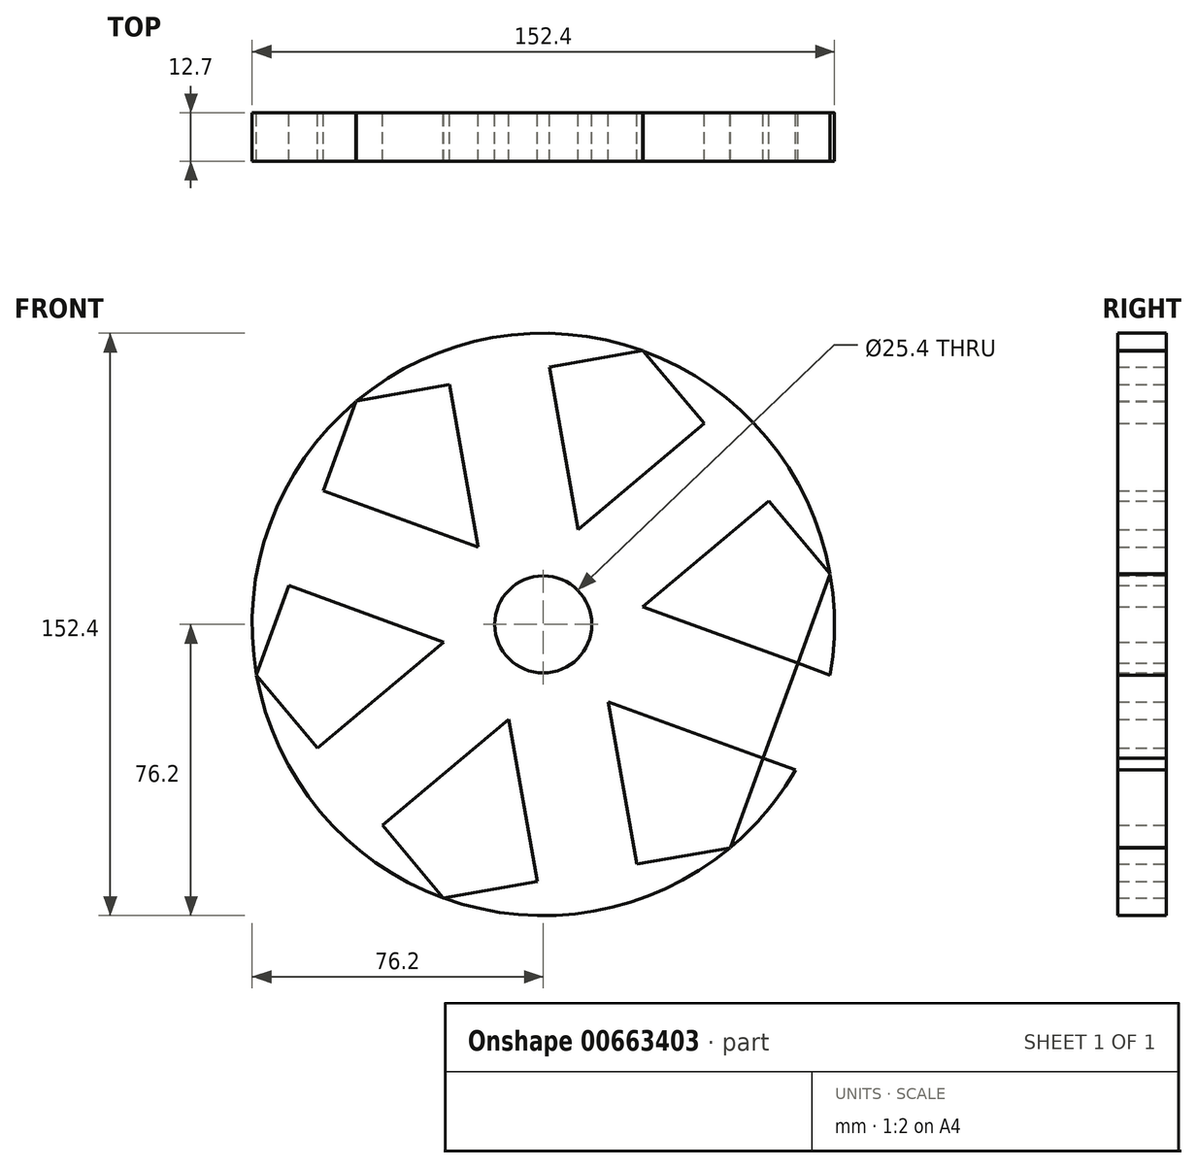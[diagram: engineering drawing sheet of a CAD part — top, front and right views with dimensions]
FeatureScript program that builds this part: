
annotation { "Feature Type Name" : "Feature", "Feature Type Description" : "" }
export const myFeature = defineFeature(function(context is Context, id is Id, definition is map)
    precondition{}
    {
        {
            var Q0;
            Q0=qCreatedBy(makeId("Front.planeOp"),FACE);
            var sketch = newSketch(context, id + "F0", { "sketchPlane" : qUnion([Q0])});
            skCircle(sketch, "E0", {"center": v(0, 0) * mm, "radius": 76.2 * mm});
            skArc(sketch, "E1", {"start": v(-12.66, 75.14) * mm, "mid": v(0, 88.9) * mm, "end": v(12.66, 75.14) * mm});
            skArc(sketch, "E2.1.0", {"start": v(-37.6, 66.28) * mm, "mid": v(-30.4, 83.54) * mm, "end": v(-13.8, 74.94) * mm});
            skArc(sketch, "E2.2.0", {"start": v(-58, 49.43) * mm, "mid": v(-57.14, 68.1) * mm, "end": v(-38.6, 65.7) * mm});
            skArc(sketch, "E2.3.0", {"start": v(-71.4, 26.61) * mm, "mid": v(-76.99, 44.45) * mm, "end": v(-58.75, 48.53) * mm});
            skArc(sketch, "E2.4.0", {"start": v(-76.2, 0.58) * mm, "mid": v(-87.55, 15.44) * mm, "end": v(-71.8, 25.51) * mm});
            skArc(sketch, "E2.5.0", {"start": v(-71.8, -25.51) * mm, "mid": v(-87.55, -15.44) * mm, "end": v(-76.2, -0.58) * mm});
            skArc(sketch, "E2.6.0", {"start": v(-58.75, -48.53) * mm, "mid": v(-76.99, -44.45) * mm, "end": v(-71.4, -26.61) * mm});
            skArc(sketch, "E2.7.0", {"start": v(-38.6, -65.7) * mm, "mid": v(-57.14, -68.1) * mm, "end": v(-58, -49.43) * mm});
            skArc(sketch, "E2.8.0", {"start": v(-13.8, -74.94) * mm, "mid": v(-30.4, -83.54) * mm, "end": v(-37.6, -66.28) * mm});
            skArc(sketch, "E2.9.0", {"start": v(12.66, -75.14) * mm, "mid": v(0, -88.9) * mm, "end": v(-12.66, -75.14) * mm});
            skArc(sketch, "E2.10.0", {"start": v(37.6, -66.28) * mm, "mid": v(30.4, -83.54) * mm, "end": v(13.8, -74.94) * mm});
            skArc(sketch, "E2.11.0", {"start": v(58, -49.43) * mm, "mid": v(57.14, -68.1) * mm, "end": v(38.6, -65.7) * mm});
            skArc(sketch, "E2.12.0", {"start": v(71.4, -26.61) * mm, "mid": v(76.99, -44.45) * mm, "end": v(58.75, -48.53) * mm});
            skArc(sketch, "E3.2.13.0", {"start": v(76.2, -0.58) * mm, "mid": v(87.55, -15.44) * mm, "end": v(71.8, -25.51) * mm});
            skArc(sketch, "E3.2.14.0", {"start": v(71.8, 25.51) * mm, "mid": v(87.55, 15.44) * mm, "end": v(76.2, 0.58) * mm});
            skArc(sketch, "E3.2.15.0", {"start": v(58.75, 48.53) * mm, "mid": v(76.99, 44.45) * mm, "end": v(71.4, 26.61) * mm});
            skArc(sketch, "E4.2.16.0", {"start": v(38.6, 65.7) * mm, "mid": v(57.14, 68.1) * mm, "end": v(58, 49.43) * mm});
            skArc(sketch, "E4.2.17.0", {"start": v(13.8, 74.94) * mm, "mid": v(30.4, 83.54) * mm, "end": v(37.6, 66.28) * mm});
            skLineSegment(sketch, "E5.0", {"start": v(26.12, 71.63) * mm, "end": v(75.1, 13.2) * mm});
            skLineSegment(sketch, "E5.1", {"start": v(75.1, 13.2) * mm, "end": v(48.97, -58.44) * mm});
            skLineSegment(sketch, "E5.2", {"start": v(48.97, -58.44) * mm, "end": v(-26.12, -71.63) * mm});
            skLineSegment(sketch, "E5.3", {"start": v(-26.12, -71.63) * mm, "end": v(-75.1, -13.2) * mm});
            skLineSegment(sketch, "E5.4", {"start": v(-75.1, -13.2) * mm, "end": v(-48.97, 58.44) * mm});
            skLineSegment(sketch, "E5.5", {"start": v(-48.97, 58.44) * mm, "end": v(26.12, 71.63) * mm});
            skCircle(sketch, "E6", {"center": v(0, 0) * mm, "radius": 12.7 * mm});
            skPoint(sketch, "E7", {"position": v(-17.01, 20.27) * mm});
            skPoint(sketch, "E8", {"position": v(9.05, 24.87) * mm});
            skPoint(sketch, "E9", {"position": v(26.06, 4.6) * mm});
            skPoint(sketch, "E10", {"position": v(-26.06, -4.6) * mm});
            skPoint(sketch, "E11", {"position": v(-9.05, -24.87) * mm});
            skPoint(sketch, "E12", {"position": v(17.01, -20.27) * mm});
            skLineSegment(sketch, "E13", {"start": v(-75.04, 13.23) * mm, "end": v(-26.06, -4.6) * mm});
            skLineSegment(sketch, "E14", {"start": v(17.01, -20.27) * mm, "end": v(66, -38.1) * mm});
            skLineSegment(sketch, "E15", {"start": v(26.06, 4.6) * mm, "end": v(75.04, -13.23) * mm});
            skLineSegment(sketch, "E16", {"start": v(26.06, 4.6) * mm, "end": v(66, 38.1) * mm});
            skLineSegment(sketch, "E17", {"start": v(9.05, 24.87) * mm, "end": v(48.98, 58.37) * mm});
            skLineSegment(sketch, "E18", {"start": v(9.05, 24.87) * mm, "end": v(0, 76.2) * mm});
            skLineSegment(sketch, "E19", {"start": v(-26.06, 71.6) * mm, "end": v(-17.01, 20.27) * mm});
            skLineSegment(sketch, "E20", {"start": v(-66, 38.1) * mm, "end": v(-17.01, 20.27) * mm});
            skLineSegment(sketch, "E21", {"start": v(-66, -38.1) * mm, "end": v(-26.06, -4.6) * mm});
            skLineSegment(sketch, "E22", {"start": v(-48.98, -58.37) * mm, "end": v(-9.05, -24.87) * mm});
            skLineSegment(sketch, "E23", {"start": v(0, -76.2) * mm, "end": v(-9.05, -24.87) * mm});
            skLineSegment(sketch, "E24", {"start": v(26.06, -71.6) * mm, "end": v(17.01, -20.27) * mm});
            skLineSegment(sketch, "E25.0", {"start": v(25.8, 4.31) * mm, "end": v(16.64, -20.2) * mm});
            skLineSegment(sketch, "E25.1", {"start": v(16.64, -20.2) * mm, "end": v(-9.17, -24.5) * mm});
            skLineSegment(sketch, "E25.2", {"start": v(-9.17, -24.5) * mm, "end": v(-25.8, -4.31) * mm});
            skLineSegment(sketch, "E25.3", {"start": v(-25.8, -4.31) * mm, "end": v(-16.64, 20.2) * mm});
            skLineSegment(sketch, "E25.4", {"start": v(-16.64, 20.2) * mm, "end": v(9.17, 24.5) * mm});
            skLineSegment(sketch, "E25.5", {"start": v(9.17, 24.5) * mm, "end": v(25.8, 4.31) * mm});
            skPoint(sketch, "E25.0.midPoint", {"position": v(21.22, -7.94) * mm});
            skPoint(sketch, "E26", {"position": v(-59.08, -32.3) * mm});
            skPoint(sketch, "E27", {"position": v(-57.52, 35.02) * mm});
            skPoint(sketch, "E28", {"position": v(1.57, 67.32) * mm});
            skPoint(sketch, "E29", {"position": v(59.08, 32.3) * mm});
            skPoint(sketch, "E30", {"position": v(57.52, -35.02) * mm});
            skPoint(sketch, "E31", {"position": v(-1.57, -67.32) * mm});
            skSolve(sketch);
        }
        {
            var Q0;
            {var subQ0=sQuery(id+"F0.wireOp",EDGE,"E2.4.0");Q0=makeQuery(id+"F0.imprint","IMPRINT",FACE,{"disambiguationData":[TD([[makeQuery(id+"F0.imprint","IMPRINT",EDGE,{"derivedFrom":subQ0}),-1.0]])]});}
            var Q1;
            {var subQ0=sQuery(id+"F0.wireOp",EDGE,"E2.3.0");Q1=makeQuery(id+"F0.imprint","IMPRINT",FACE,{"disambiguationData":[TD([[makeQuery(id+"F0.imprint","IMPRINT",EDGE,{"derivedFrom":subQ0}),-1.0]])]});}
            var Q2;
            {var subQ5=sQuery(id+"F0.wireOp",EDGE,"E2.2.0");Q2=makeQuery(id+"F0.imprint","IMPRINT",FACE,{"disambiguationData":[TD([[makeQuery(id+"F0.imprint","IMPRINT",EDGE,{"derivedFrom":subQ5}),-1.0]])]});}
            var Q3;
            {var subQ0=sQuery(id+"F0.wireOp",EDGE,"E1");Q3=makeQuery(id+"F0.imprint","IMPRINT",FACE,{"disambiguationData":[TD([[makeQuery(id+"F0.imprint","IMPRINT",EDGE,{"derivedFrom":subQ0}),-1.0]])]});}
            var Q4;
            {var subQ0=sQuery(id+"F0.wireOp",EDGE,"E2.1.0");Q4=makeQuery(id+"F0.imprint","IMPRINT",FACE,{"disambiguationData":[TD([[makeQuery(id+"F0.imprint","IMPRINT",EDGE,{"derivedFrom":subQ0}),-1.0]])]});}
            var Q5;
            Q5=makeQuery(id+"F0.imprint","IMPRINT",FACE,{"disambiguationData":[TD([[makeQuery(id+"F0.imprint","IMPRINT",EDGE,{"derivedFrom":sQuery(id+"F0.wireOp",EDGE,"E6")}),-1.0]])]});
            var Q6;
            Q6=makeQuery(id+"F0.imprint","IMPRINT",FACE,{"disambiguationData":[TD([[makeQuery(id+"F0.imprint","IMPRINT",EDGE,{"derivedFrom":sQuery(id+"F0.wireOp",EDGE,"E25.0")}),1.0]])]});
            var Q7;
            {var subQ0=sQuery(id+"F0.wireOp",EDGE,"E0");var subQ4=makeQuery(id+"F0.imprint","INTERSECT",VERTEX,{"disambiguationData":[OD(0.0)],"derivedFrom":[subQ0,sQuery(id+"F0.wireOp",EDGE,"E2.3.0")]});Q7=makeQuery(id+"F0.imprint","IMPRINT",FACE,{"disambiguationData":[TD([[makeQuery(id+"F0.imprint","IMPRINT",EDGE,{"disambiguationData":[TD([[subQ4,1.0]])],"derivedFrom":subQ0}),1.0]])]});}
            var Q8;
            {var subQ0=sQuery(id+"F0.wireOp",EDGE,"E0");var subQ6=makeQuery(id+"F0.imprint","INTERSECT",VERTEX,{"disambiguationData":[OD(0.0)],"derivedFrom":[subQ0,sQuery(id+"F0.wireOp",EDGE,"E2.4.0")]});Q8=makeQuery(id+"F0.imprint","IMPRINT",FACE,{"disambiguationData":[TD([[makeQuery(id+"F0.imprint","IMPRINT",EDGE,{"disambiguationData":[TD([[subQ6,1.0]])],"derivedFrom":subQ0}),1.0]])]});}
            var Q9;
            {var subQ1=sQuery(id+"F0.wireOp",EDGE,"E0");var subQ7=makeQuery(id+"F0.imprint","INTERSECT",VERTEX,{"disambiguationData":[OD(0.0)],"derivedFrom":[subQ1,sQuery(id+"F0.wireOp",EDGE,"E2.5.0")]});Q9=makeQuery(id+"F0.imprint","IMPRINT",FACE,{"disambiguationData":[TD([[makeQuery(id+"F0.imprint","IMPRINT",EDGE,{"disambiguationData":[TD([[subQ7,1.0]])],"derivedFrom":subQ1}),1.0]])]});}
            var Q10;
            {var subQ1=sQuery(id+"F0.wireOp",EDGE,"E0");var subQ7=makeQuery(id+"F0.imprint","INTERSECT",VERTEX,{"disambiguationData":[OD(0.0)],"derivedFrom":[subQ1,sQuery(id+"F0.wireOp",EDGE,"E2.2.0")]});Q10=makeQuery(id+"F0.imprint","IMPRINT",FACE,{"disambiguationData":[TD([[makeQuery(id+"F0.imprint","IMPRINT",EDGE,{"disambiguationData":[TD([[subQ7,1.0]])],"derivedFrom":subQ1}),1.0]])]});}
            var Q11;
            {var subQ0=sQuery(id+"F0.wireOp",EDGE,"E0");var subQ6=makeQuery(id+"F0.imprint","INTERSECT",VERTEX,{"disambiguationData":[OD(0.0)],"derivedFrom":[subQ0,sQuery(id+"F0.wireOp",EDGE,"E2.1.0")]});Q11=makeQuery(id+"F0.imprint","IMPRINT",FACE,{"disambiguationData":[TD([[makeQuery(id+"F0.imprint","IMPRINT",EDGE,{"disambiguationData":[TD([[subQ6,1.0]])],"derivedFrom":subQ0}),1.0]])]});}
            var Q12;
            {var subQ1=sQuery(id+"F0.wireOp",EDGE,"E0");var subQ7=makeQuery(id+"F0.imprint","INTERSECT",VERTEX,{"disambiguationData":[OD(0.0)],"derivedFrom":[subQ1,sQuery(id+"F0.wireOp",EDGE,"E4.2.17.0")]});Q12=makeQuery(id+"F0.imprint","IMPRINT",FACE,{"disambiguationData":[TD([[makeQuery(id+"F0.imprint","IMPRINT",EDGE,{"disambiguationData":[TD([[subQ7,1.0]])],"derivedFrom":subQ1}),1.0]])]});}
            var Q13;
            {var subQ5=sQuery(id+"F0.wireOp",EDGE,"E2.5.0");Q13=makeQuery(id+"F0.imprint","IMPRINT",FACE,{"disambiguationData":[TD([[makeQuery(id+"F0.imprint","IMPRINT",EDGE,{"derivedFrom":subQ5}),-1.0]])]});}
            var Q14;
            {var subQ5=sQuery(id+"F0.wireOp",EDGE,"E4.2.17.0");Q14=makeQuery(id+"F0.imprint","IMPRINT",FACE,{"disambiguationData":[TD([[makeQuery(id+"F0.imprint","IMPRINT",EDGE,{"derivedFrom":subQ5}),-1.0]])]});}
            var Q15;
            {var subQ0=sQuery(id+"F0.wireOp",EDGE,"E4.2.16.0");Q15=makeQuery(id+"F0.imprint","IMPRINT",FACE,{"disambiguationData":[TD([[makeQuery(id+"F0.imprint","IMPRINT",EDGE,{"derivedFrom":subQ0}),-1.0]])]});}
            var Q16;
            {var subQ0=sQuery(id+"F0.wireOp",EDGE,"E0");var subQ6=makeQuery(id+"F0.imprint","INTERSECT",VERTEX,{"disambiguationData":[OD(0.0)],"derivedFrom":[subQ0,sQuery(id+"F0.wireOp",EDGE,"E4.2.16.0")]});Q16=makeQuery(id+"F0.imprint","IMPRINT",FACE,{"disambiguationData":[TD([[makeQuery(id+"F0.imprint","IMPRINT",EDGE,{"disambiguationData":[TD([[subQ6,1.0]])],"derivedFrom":subQ0}),1.0]])]});}
            var Q17;
            {var subQ0=sQuery(id+"F0.wireOp",EDGE,"E2.6.0");Q17=makeQuery(id+"F0.imprint","IMPRINT",FACE,{"disambiguationData":[TD([[makeQuery(id+"F0.imprint","IMPRINT",EDGE,{"derivedFrom":subQ0}),-1.0]])]});}
            var Q18;
            {var subQ1=sQuery(id+"F0.wireOp",EDGE,"E0");var subQ7=makeQuery(id+"F0.imprint","INTERSECT",VERTEX,{"disambiguationData":[OD(0.0)],"derivedFrom":[subQ1,sQuery(id+"F0.wireOp",EDGE,"E2.8.0")]});Q18=makeQuery(id+"F0.imprint","IMPRINT",FACE,{"disambiguationData":[TD([[makeQuery(id+"F0.imprint","IMPRINT",EDGE,{"disambiguationData":[TD([[subQ7,1.0]])],"derivedFrom":subQ1}),1.0]])]});}
            var Q19;
            {var subQ0=sQuery(id+"F0.wireOp",EDGE,"E2.9.0");Q19=makeQuery(id+"F0.imprint","IMPRINT",FACE,{"disambiguationData":[TD([[makeQuery(id+"F0.imprint","IMPRINT",EDGE,{"derivedFrom":subQ0}),-1.0]])]});}
            var Q20;
            {var subQ0=sQuery(id+"F0.wireOp",EDGE,"E2.10.0");Q20=makeQuery(id+"F0.imprint","IMPRINT",FACE,{"disambiguationData":[TD([[makeQuery(id+"F0.imprint","IMPRINT",EDGE,{"derivedFrom":subQ0}),-1.0]])]});}
            var Q21;
            {var subQ0=sQuery(id+"F0.wireOp",EDGE,"E0");var subQ6=makeQuery(id+"F0.imprint","INTERSECT",VERTEX,{"disambiguationData":[OD(0.0)],"derivedFrom":[subQ0,sQuery(id+"F0.wireOp",EDGE,"E2.10.0")]});Q21=makeQuery(id+"F0.imprint","IMPRINT",FACE,{"disambiguationData":[TD([[makeQuery(id+"F0.imprint","IMPRINT",EDGE,{"disambiguationData":[TD([[subQ6,1.0]])],"derivedFrom":subQ0}),1.0]])]});}
            var Q22;
            {var subQ0=sQuery(id+"F0.wireOp",EDGE,"E2.8.0");Q22=makeQuery(id+"F0.imprint","IMPRINT",FACE,{"disambiguationData":[TD([[makeQuery(id+"F0.imprint","IMPRINT",EDGE,{"derivedFrom":subQ0}),-1.0]])]});}
            var Q23;
            {var subQ0=sQuery(id+"F0.wireOp",EDGE,"E2.7.0");Q23=makeQuery(id+"F0.imprint","IMPRINT",FACE,{"disambiguationData":[TD([[makeQuery(id+"F0.imprint","IMPRINT",EDGE,{"derivedFrom":subQ0}),-1.0]])]});}
            var Q24;
            {var subQ0=sQuery(id+"F0.wireOp",EDGE,"E0");var subQ6=makeQuery(id+"F0.imprint","INTERSECT",VERTEX,{"disambiguationData":[OD(0.0)],"derivedFrom":[subQ0,sQuery(id+"F0.wireOp",EDGE,"E2.7.0")]});Q24=makeQuery(id+"F0.imprint","IMPRINT",FACE,{"disambiguationData":[TD([[makeQuery(id+"F0.imprint","IMPRINT",EDGE,{"disambiguationData":[TD([[subQ6,1.0]])],"derivedFrom":subQ0}),1.0]])]});}
            var Q25;
            {var subQ0=sQuery(id+"F0.wireOp",EDGE,"E2.11.0");Q25=makeQuery(id+"F0.imprint","IMPRINT",FACE,{"disambiguationData":[TD([[makeQuery(id+"F0.imprint","IMPRINT",EDGE,{"derivedFrom":subQ0}),-1.0]])]});}
            var Q26;
            {var subQ0=sQuery(id+"F0.wireOp",EDGE,"E2.12.0");Q26=makeQuery(id+"F0.imprint","IMPRINT",FACE,{"disambiguationData":[TD([[makeQuery(id+"F0.imprint","IMPRINT",EDGE,{"derivedFrom":subQ0}),-1.0]])]});}
            var Q27;
            {var subQ1=sQuery(id+"F0.wireOp",EDGE,"E0");var subQ5=makeQuery(id+"F0.imprint","INTERSECT",VERTEX,{"disambiguationData":[OD(0.0)],"derivedFrom":[subQ1,sQuery(id+"F0.wireOp",EDGE,"E2.11.0")]});Q27=makeQuery(id+"F0.imprint","IMPRINT",FACE,{"disambiguationData":[TD([[makeQuery(id+"F0.imprint","IMPRINT",EDGE,{"disambiguationData":[TD([[subQ5,1.0]])],"derivedFrom":subQ1}),1.0]])]});}
            var Q28;
            {var subQ1=sQuery(id+"F0.wireOp",EDGE,"E0");var subQ6=makeQuery(id+"F0.imprint","INTERSECT",VERTEX,{"disambiguationData":[OD(1.0)],"derivedFrom":[subQ1,sQuery(id+"F0.wireOp",EDGE,"E3.2.14.0")]});Q28=makeQuery(id+"F0.imprint","IMPRINT",FACE,{"disambiguationData":[TD([[makeQuery(id+"F0.imprint","IMPRINT",EDGE,{"disambiguationData":[TD([[subQ6,-1.0]])],"derivedFrom":subQ1}),1.0]])]});}
            var Q29;
            {var subQ1=sQuery(id+"F0.wireOp",EDGE,"E0");var subQ7=makeQuery(id+"F0.imprint","INTERSECT",VERTEX,{"disambiguationData":[OD(0.0)],"derivedFrom":[subQ1,sQuery(id+"F0.wireOp",EDGE,"E3.2.14.0")]});Q29=makeQuery(id+"F0.imprint","IMPRINT",FACE,{"disambiguationData":[TD([[makeQuery(id+"F0.imprint","IMPRINT",EDGE,{"disambiguationData":[TD([[subQ7,1.0]])],"derivedFrom":subQ1}),1.0]])]});}
            var Q30;
            {var subQ0=sQuery(id+"F0.wireOp",EDGE,"E3.2.15.0");Q30=makeQuery(id+"F0.imprint","IMPRINT",FACE,{"disambiguationData":[TD([[makeQuery(id+"F0.imprint","IMPRINT",EDGE,{"derivedFrom":subQ0}),-1.0]])]});}
            var Q31;
            {var subQ0=sQuery(id+"F0.wireOp",EDGE,"E3.2.14.0");Q31=makeQuery(id+"F0.imprint","IMPRINT",FACE,{"disambiguationData":[TD([[makeQuery(id+"F0.imprint","IMPRINT",EDGE,{"derivedFrom":subQ0}),-1.0]])]});}
            var Q32;
            {var subQ0=sQuery(id+"F0.wireOp",EDGE,"E3.2.13.0");Q32=makeQuery(id+"F0.imprint","IMPRINT",FACE,{"disambiguationData":[TD([[makeQuery(id+"F0.imprint","IMPRINT",EDGE,{"derivedFrom":subQ0}),-1.0]])]});}
            var Q33;
            {var subQ0=sQuery(id+"F0.wireOp",EDGE,"E0");var subQ4=makeQuery(id+"F0.imprint","INTERSECT",VERTEX,{"disambiguationData":[OD(0.0)],"derivedFrom":[subQ0,sQuery(id+"F0.wireOp",EDGE,"E3.2.15.0")]});Q33=makeQuery(id+"F0.imprint","IMPRINT",FACE,{"disambiguationData":[TD([[makeQuery(id+"F0.imprint","IMPRINT",EDGE,{"disambiguationData":[TD([[subQ4,1.0]])],"derivedFrom":subQ0}),1.0]])]});}
            var Q34;
            {var subQ0=sQuery(id+"F0.wireOp",EDGE,"E0");var subQ8=makeQuery(id+"F0.imprint","INTERSECT",VERTEX,{"disambiguationData":[OD(0.0)],"derivedFrom":[subQ0,sQuery(id+"F0.wireOp",EDGE,"E2.12.0")]});Q34=makeQuery(id+"F0.imprint","IMPRINT",FACE,{"disambiguationData":[TD([[makeQuery(id+"F0.imprint","IMPRINT",EDGE,{"disambiguationData":[TD([[subQ8,1.0]])],"derivedFrom":subQ0}),1.0]])]});}
            var Q35;
            {var subQ0=sQuery(id+"F0.wireOp",EDGE,"E0");var subQ4=makeQuery(id+"F0.imprint","INTERSECT",VERTEX,{"disambiguationData":[OD(0.0)],"derivedFrom":[subQ0,sQuery(id+"F0.wireOp",EDGE,"E2.9.0")]});Q35=makeQuery(id+"F0.imprint","IMPRINT",FACE,{"disambiguationData":[TD([[makeQuery(id+"F0.imprint","IMPRINT",EDGE,{"disambiguationData":[TD([[subQ4,1.0]])],"derivedFrom":subQ0}),1.0]])]});}
            var Q36;
            {var subQ0=sQuery(id+"F0.wireOp",EDGE,"E0");var subQ8=makeQuery(id+"F0.imprint","INTERSECT",VERTEX,{"disambiguationData":[OD(0.0)],"derivedFrom":[subQ0,sQuery(id+"F0.wireOp",EDGE,"E2.6.0")]});Q36=makeQuery(id+"F0.imprint","IMPRINT",FACE,{"disambiguationData":[TD([[makeQuery(id+"F0.imprint","IMPRINT",EDGE,{"disambiguationData":[TD([[subQ8,1.0]])],"derivedFrom":subQ0}),1.0]])]});}
            var Q37;
            {var subQ0=sQuery(id+"F0.wireOp",EDGE,"E0");var subQ8=makeQuery(id+"F0.imprint","INTERSECT",VERTEX,{"disambiguationData":[OD(0.0)],"derivedFrom":[subQ0,sQuery(id+"F0.wireOp",EDGE,"E1")]});Q37=makeQuery(id+"F0.imprint","IMPRINT",FACE,{"disambiguationData":[TD([[makeQuery(id+"F0.imprint","IMPRINT",EDGE,{"disambiguationData":[TD([[subQ8,1.0]])],"derivedFrom":subQ0}),1.0]])]});}
            extrude(context, id + "F1", {"entities" : qUnion([Q0, Q1, Q2, Q3, Q4, Q5, Q6, Q7, Q8, Q9, Q10, Q11, Q12, Q13, Q14, Q15, Q16, Q17, Q18, Q19, Q20, Q21, Q22, Q23, Q24, Q25, Q26, Q27, Q28, Q29, Q30, Q31, Q32, Q33, Q34, Q35, Q36, Q37]), "endBound" : BoundingType.SYMMETRIC, "depth" : 12.7 * mm, "offsetDistance" : 25.4 * mm});
        }
    });
